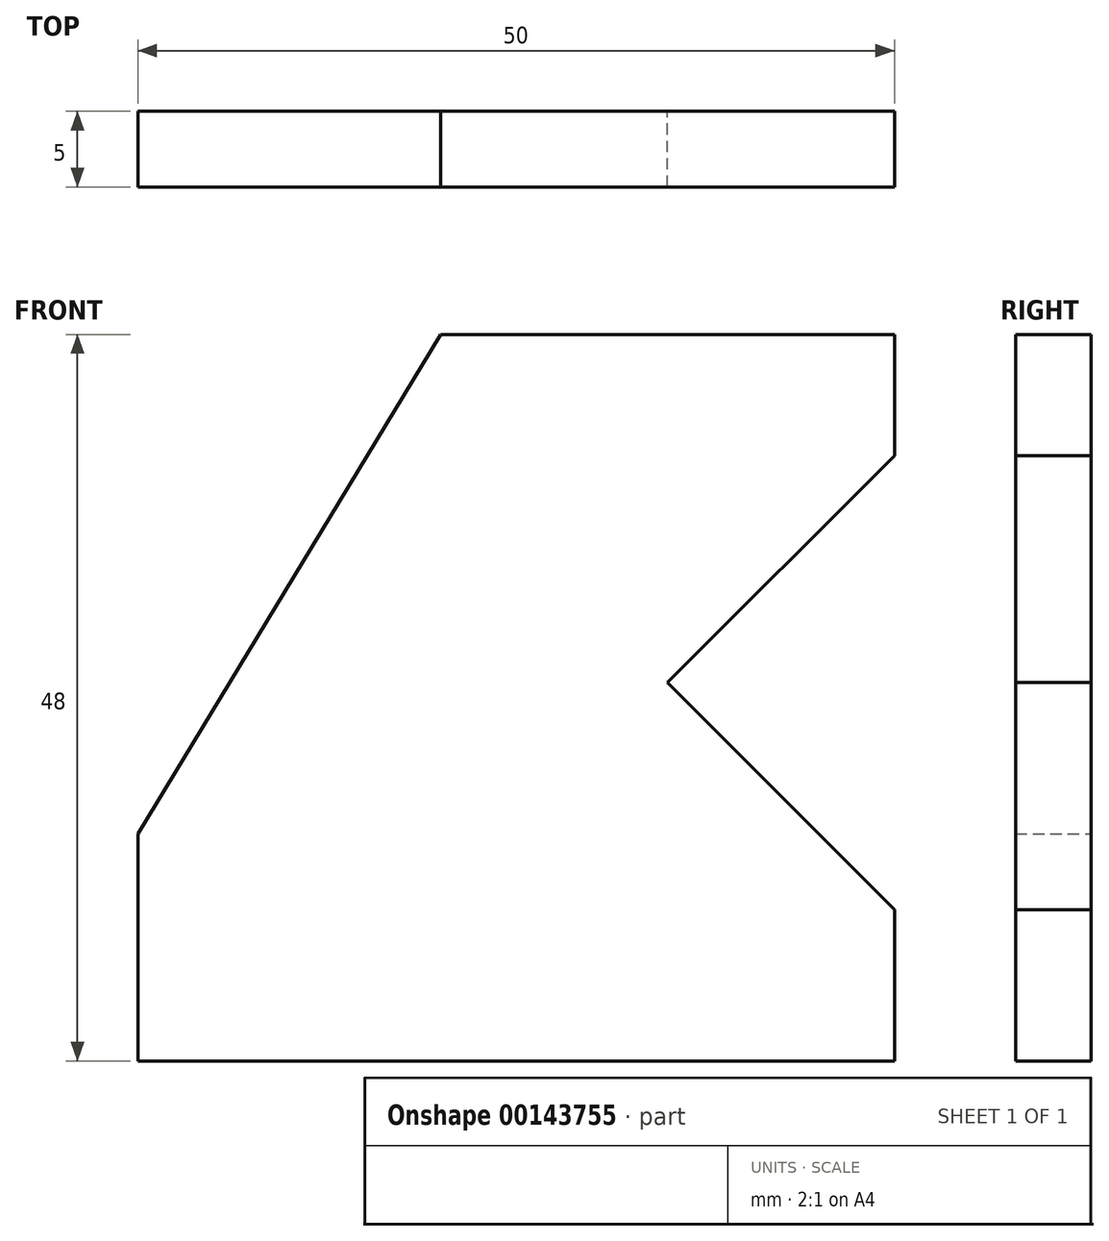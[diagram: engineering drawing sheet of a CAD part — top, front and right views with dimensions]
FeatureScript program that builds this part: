
annotation { "Feature Type Name" : "Feature", "Feature Type Description" : "" }
export const myFeature = defineFeature(function(context is Context, id is Id, definition is map)
    precondition{}
    {
        {
            var Q0;
            Q0=qCreatedBy(makeId("Front.planeOp"),FACE);
            var sketch = newSketch(context, id + "F0", { "sketchPlane" : qUnion([Q0])});
            skLineSegment(sketch, "E0", {"start": v(0, 0) * mm, "end": v(0, 15) * mm});
            skLineSegment(sketch, "E1", {"start": v(0, 15) * mm, "end": v(20, 48) * mm});
            skLineSegment(sketch, "E2", {"start": v(20, 48) * mm, "end": v(50, 48) * mm});
            skLineSegment(sketch, "E3", {"start": v(50, 48) * mm, "end": v(50, 40) * mm});
            skLineSegment(sketch, "E4", {"start": v(50, 40) * mm, "end": v(35, 25) * mm});
            skLineSegment(sketch, "E5", {"start": v(35, 25) * mm, "end": v(50, 10) * mm});
            skLineSegment(sketch, "E6", {"start": v(50, 10) * mm, "end": v(50, 0) * mm});
            skLineSegment(sketch, "E7", {"start": v(50, 0) * mm, "end": v(0, 0) * mm});
            skLineSegment(sketch, "E8", {"start": v(25.68, 25) * mm, "end": v(50.47, 25) * mm, "construction": true});
            skSolve(sketch);
        }
        {
            var Q0;
            Q0=qSketchRegion(id+"F0",true);
            extrude(context, id + "F1", {"entities" : qUnion([Q0]), "depth" : 5 * mm});
        }
    });
